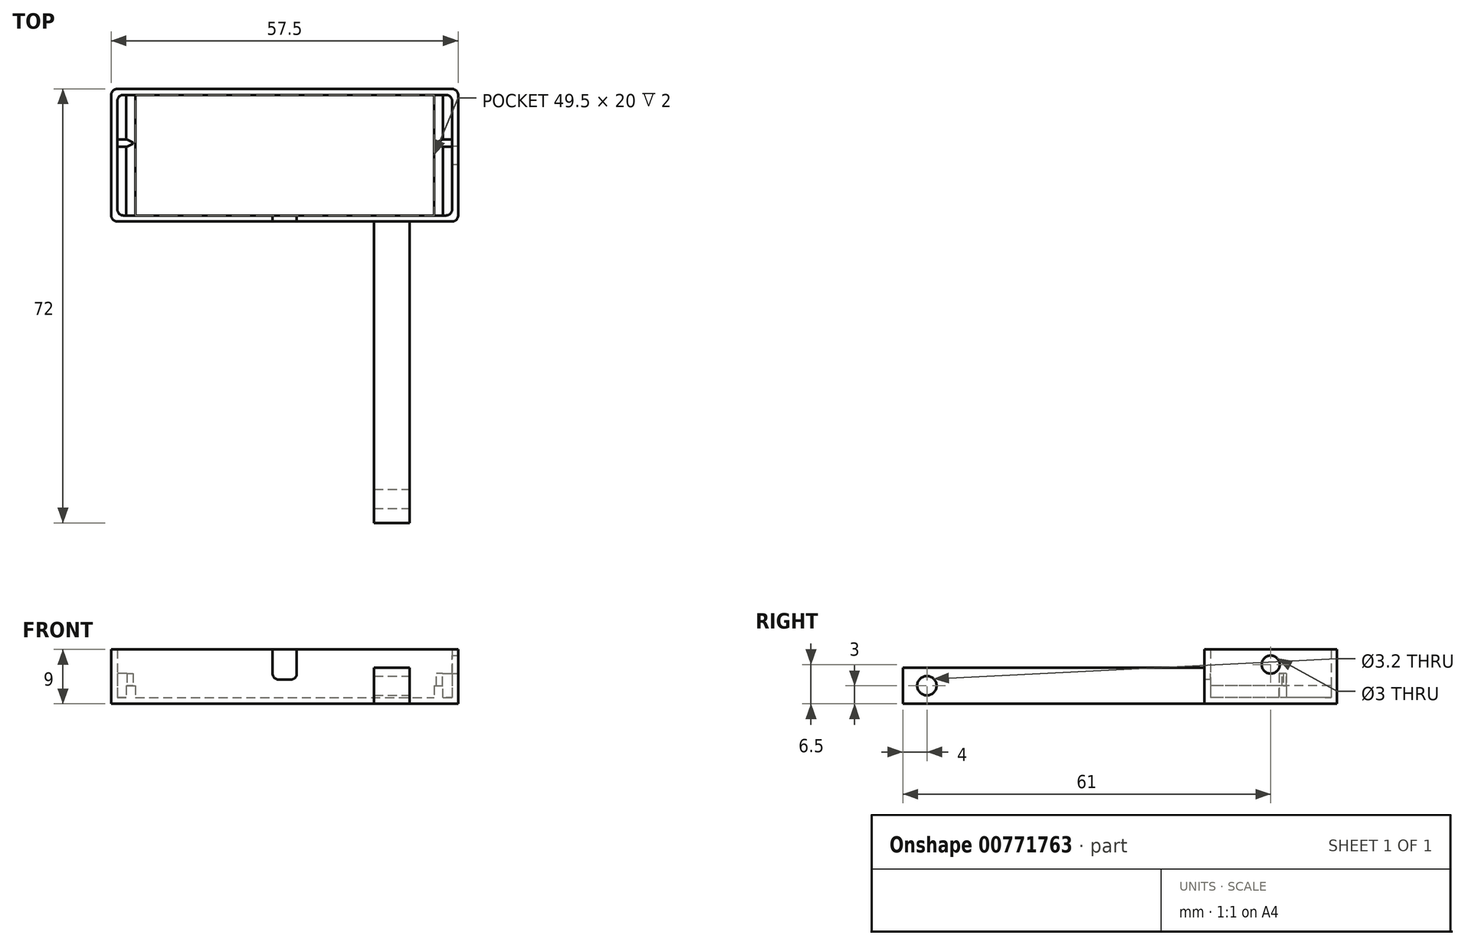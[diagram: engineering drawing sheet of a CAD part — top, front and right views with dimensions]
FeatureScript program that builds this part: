
annotation { "Feature Type Name" : "Feature", "Feature Type Description" : "" }
export const myFeature = defineFeature(function(context is Context, id is Id, definition is map)
    precondition{}
    {
        {
            var Q0;
            Q0=qCreatedBy(makeId("Top.planeOp"),FACE);
            var sketch = newSketch(context, id + "F0", { "sketchPlane" : qUnion([Q0])});
            skLineSegment(sketch, "E0.bottom", {"start": v(-27.75, 10) * mm, "end": v(27.75, 10) * mm});
            skLineSegment(sketch, "E0.top", {"start": v(-27.75, -10) * mm, "end": v(27.75, -10) * mm});
            skLineSegment(sketch, "E0.left", {"start": v(-27.75, 10) * mm, "end": v(-27.75, -10) * mm});
            skLineSegment(sketch, "E0.right", {"start": v(27.75, 10) * mm, "end": v(27.75, -10) * mm});
            skLineSegment(sketch, "E1", {"start": v(0, 10) * mm, "end": v(0, -10) * mm, "construction": true});
            skLineSegment(sketch, "E2", {"start": v(-27.75, 0) * mm, "end": v(27.75, 0) * mm, "construction": true});
            skLineSegment(sketch, "E3.0", {"start": v(-28.75, 11) * mm, "end": v(28.75, 11) * mm});
            skLineSegment(sketch, "E3.1", {"start": v(-28.75, 11) * mm, "end": v(-28.75, -11) * mm});
            skLineSegment(sketch, "E3.2", {"start": v(-28.75, -11) * mm, "end": v(28.75, -11) * mm});
            skLineSegment(sketch, "E3.3", {"start": v(28.75, 11) * mm, "end": v(28.75, -11) * mm});
            skSolve(sketch);
        }
        {
            var Q0;
            Q0 = qSketchRegion(id + "F0", true);
            extrude(context, id + "F1", {"entities" : qUnion([Q0]), "depth" : 9 * mm, "offsetDistance" : 25 * mm});
        }
        {
            var Q0;
            Q0=qCreatedBy(makeId("Top.planeOp"),FACE);
            var sketch = newSketch(context, id + "F2", { "sketchPlane" : qUnion([Q0])});
            skLineSegment(sketch, "E4.bottom", {"start": v(-28.75, 11) * mm, "end": v(28.75, 11) * mm});
            skLineSegment(sketch, "E4.top", {"start": v(-28.75, -11) * mm, "end": v(28.75, -11) * mm});
            skLineSegment(sketch, "E4.left", {"start": v(-28.75, 11) * mm, "end": v(-28.75, -11) * mm});
            skLineSegment(sketch, "E4.right", {"start": v(28.75, 11) * mm, "end": v(28.75, -11) * mm});
            skSolve(sketch);
        }
        {
            var Q0;
            Q0 = qSketchRegion(id + "F2", true);
            extrude(context, id + "F3", {"entities" : qUnion([Q0]), "operationType" : NewBodyOperationType.ADD, "depth" : 1 * mm, "offsetDistance" : 25 * mm});
        }
        {
            var Q0;
            Q0=makeQuery(id+"F1.opExtrude","SWEPT_FACE",FACE,{"disambiguationData":[OSD([sQuery(id+"F0.wireOp",EDGE,"E3.2")])]});
            var sketch = newSketch(context, id + "F4", { "sketchPlane" : qUnion([Q0])});
            skLineSegment(sketch, "E5", {"start": v(-2, 9) * mm, "end": v(-2, 5) * mm});
            skLineSegment(sketch, "E6.MirrorCS", {"start": v(2, 9) * mm, "end": v(2, 5) * mm});
            skLineSegment(sketch, "E7", {"start": v(-1, 4) * mm, "end": v(1, 4) * mm});
            skPoint(sketch, "E8.visualSharp", {"position": v(-2, 4) * mm});
            skArc(sketch, "E8.filletArc", {"start": v(-2, 5) * mm, "mid": v(-1.7, 4.3) * mm, "end": v(-1, 4) * mm});
            skPoint(sketch, "E9.visualSharp", {"position": v(2, 4) * mm});
            skArc(sketch, "E9.filletArc", {"start": v(1, 4) * mm, "mid": v(1.7, 4.3) * mm, "end": v(2, 5) * mm});
            skLineSegment(sketch, "E10", {"start": v(2, 9) * mm, "end": v(-2, 9) * mm});
            skSolve(sketch);
        }
        {
            var Q0;
            Q0 = qSketchRegion(id + "F4", true);
            var Q1;
            Q1=makeQuery(id+"F1.opExtrude","SWEPT_FACE",FACE,{"disambiguationData":[OSD([sQuery(id+"F0.wireOp",EDGE,"E0.top")])]});
            extrude(context, id + "F5", {"entities" : qUnion([Q0]), "operationType" : NewBodyOperationType.REMOVE, "endBound" : BoundingType.UP_TO_SURFACE, "oppositeDirection" : true, "depth" : 25 * mm, "endBoundEntityFace" : qUnion([Q1]), "offsetDistance" : 25 * mm});
        }
        {
            var Q0;
            Q0=makeQuery(id+"F1.opExtrude","SWEPT_FACE",FACE,{"disambiguationData":[OSD([sQuery(id+"F0.wireOp",EDGE,"E3.2")])]});
            var sketch = newSketch(context, id + "F6", { "sketchPlane" : qUnion([Q0])});
            skLineSegment(sketch, "E11", {"start": v(17.75, 9) * mm, "end": v(17.75, 0) * mm, "construction": true});
            skLineSegment(sketch, "E12", {"start": v(14.8, 6) * mm, "end": v(14.8, 0) * mm});
            skLineSegment(sketch, "E13.MirrorCS", {"start": v(20.7, 6) * mm, "end": v(20.7, 0) * mm});
            skLineSegment(sketch, "E14", {"start": v(14.8, 6) * mm, "end": v(20.7, 6) * mm});
            skLineSegment(sketch, "E15", {"start": v(20.7, 0) * mm, "end": v(14.8, 0) * mm});
            skSolve(sketch);
        }
        {
            var Q0;
            Q0 = qSketchRegion(id + "F6", true);
            extrude(context, id + "F7", {"entities" : qUnion([Q0]), "operationType" : NewBodyOperationType.ADD, "depth" : 50 * mm, "offsetDistance" : 25 * mm});
        }
        {
            var Q0;
            Q0=makeQuery(id+"F7.opExtrude","SWEPT_FACE",FACE,{"disambiguationData":[OSD([sQuery(id+"F6.wireOp",EDGE,"E13.MirrorCS")])]});
            var sketch = newSketch(context, id + "F8", { "sketchPlane" : qUnion([Q0])});
            skCircle(sketch, "E16", {"center": v(-57, 3) * mm, "radius": 1.6 * mm});
            skLineSegment(sketch, "E17", {"start": v(-61, 3) * mm, "end": v(-11, 3) * mm, "construction": true});
            skSolve(sketch);
        }
        {
            var Q0;
            Q0 = qSketchRegion(id + "F8", true);
            var Q1;
            Q1=makeQuery(id+"F7.opExtrude","SWEPT_FACE",FACE,{"disambiguationData":[OSD([sQuery(id+"F6.wireOp",EDGE,"E12")])]});
            extrude(context, id + "F9", {"entities" : qUnion([Q0]), "operationType" : NewBodyOperationType.REMOVE, "endBound" : BoundingType.UP_TO_SURFACE, "oppositeDirection" : true, "depth" : 25 * mm, "endBoundEntityFace" : qUnion([Q1]), "offsetDistance" : 25 * mm});
        }
        {
            var Q0;
            Q0=makeQuery(id+"F3.opExtrude","CAP_FACE",FACE,{"disambiguationData":[OSD([sQuery(id+"F2.wireOp",EDGE,"E4.bottom"),sQuery(id+"F2.wireOp",EDGE,"E4.top"),sQuery(id+"F2.wireOp",EDGE,"E4.left"),sQuery(id+"F2.wireOp",EDGE,"E4.right")])],"isStart":false});
            var sketch = newSketch(context, id + "F10", { "sketchPlane" : qUnion([Q0])});
            skLineSegment(sketch, "E18.bottom", {"start": v(-26.25, 10) * mm, "end": v(-24.75, 10) * mm});
            skLineSegment(sketch, "E18.top", {"start": v(-26.25, -10) * mm, "end": v(-24.75, -10) * mm});
            skLineSegment(sketch, "E18.left", {"start": v(-26.25, 10) * mm, "end": v(-26.25, -10) * mm});
            skLineSegment(sketch, "E18.right", {"start": v(-24.75, 10) * mm, "end": v(-24.75, -10) * mm});
            skLineSegment(sketch, "E19.MirrorCS", {"start": v(26.25, -10) * mm, "end": v(24.75, -10) * mm});
            skLineSegment(sketch, "E20.MirrorCS", {"start": v(24.75, 10) * mm, "end": v(24.75, -10) * mm});
            skLineSegment(sketch, "E21.MirrorCS", {"start": v(26.25, 10) * mm, "end": v(26.25, -10) * mm});
            skLineSegment(sketch, "E22.MirrorCS", {"start": v(26.25, 10) * mm, "end": v(24.75, 10) * mm});
            skSolve(sketch);
        }
        {
            var Q0;
            Q0 = qSketchRegion(id + "F10", true);
            extrude(context, id + "F11", {"entities" : qUnion([Q0]), "operationType" : NewBodyOperationType.ADD, "depth" : 2 * mm, "offsetDistance" : 25 * mm});
        }
        {
            var Q0;
            Q0=makeQuery(id+"F1.opExtrude","SWEPT_EDGE",EDGE,{"disambiguationData":[OSD([sQuery(id+"F0.wireOp",EDGE,"E3.1"),sQuery(id+"F0.wireOp",EDGE,"E3.2")])]});
            var Q1;
            Q1=makeQuery(id+"F1.opExtrude","SWEPT_EDGE",EDGE,{"disambiguationData":[OSD([sQuery(id+"F0.wireOp",EDGE,"E3.2"),sQuery(id+"F0.wireOp",EDGE,"E3.3")])]});
            var Q2;
            Q2=makeQuery(id+"F1.opExtrude","SWEPT_EDGE",EDGE,{"disambiguationData":[OSD([sQuery(id+"F0.wireOp",EDGE,"E3.0"),sQuery(id+"F0.wireOp",EDGE,"E3.3")])]});
            var Q3;
            Q3=makeQuery(id+"F1.opExtrude","SWEPT_EDGE",EDGE,{"disambiguationData":[OSD([sQuery(id+"F0.wireOp",EDGE,"E3.0"),sQuery(id+"F0.wireOp",EDGE,"E3.1")])]});
            fillet(context, id + "F12", {"entities" : qUnion([Q0, Q1, Q2, Q3]), "radius" : 1 * mm, "tangentPropagation" : true, "allowEdgeOverflow" : false});
        }
        {
            var Q0;
            Q0=makeQuery(id+"F1.opExtrude","SWEPT_EDGE",EDGE,{"disambiguationData":[OSD([sQuery(id+"F0.wireOp",EDGE,"E0.bottom"),sQuery(id+"F0.wireOp",EDGE,"E0.left")])]});
            var Q1;
            Q1=makeQuery(id+"F1.opExtrude","SWEPT_EDGE",EDGE,{"disambiguationData":[OSD([sQuery(id+"F0.wireOp",EDGE,"E0.bottom"),sQuery(id+"F0.wireOp",EDGE,"E0.right")])]});
            var Q2;
            Q2=makeQuery(id+"F1.opExtrude","SWEPT_EDGE",EDGE,{"disambiguationData":[OSD([sQuery(id+"F0.wireOp",EDGE,"E0.top"),sQuery(id+"F0.wireOp",EDGE,"E0.right")])]});
            var Q3;
            Q3=makeQuery(id+"F1.opExtrude","SWEPT_EDGE",EDGE,{"disambiguationData":[OSD([sQuery(id+"F0.wireOp",EDGE,"E0.top"),sQuery(id+"F0.wireOp",EDGE,"E0.left")])]});
            fillet(context, id + "F13", {"entities" : qUnion([Q0, Q1, Q2, Q3]), "radius" : 1 * mm, "tangentPropagation" : true, "allowEdgeOverflow" : false});
        }
        {
            var Q0;
            Q0=makeQuery(id+"F1.opExtrude","SWEPT_FACE",FACE,{"disambiguationData":[OSD([sQuery(id+"F0.wireOp",EDGE,"E3.3")])]});
            var sketch = newSketch(context, id + "F14", { "sketchPlane" : qUnion([Q0])});
            skCircle(sketch, "E23", {"center": v(0, 6.5) * mm, "radius": 1.5 * mm});
            skSolve(sketch);
        }
        {
            var Q0;
            Q0 = qSketchRegion(id + "F14", true);
            var Q1;
            Q1=makeQuery(id+"F1.opExtrude","SWEPT_FACE",FACE,{"disambiguationData":[OSD([sQuery(id+"F0.wireOp",EDGE,"E0.right")])]});
            extrude(context, id + "F15", {"entities" : qUnion([Q0]), "operationType" : NewBodyOperationType.REMOVE, "endBound" : BoundingType.UP_TO_SURFACE, "oppositeDirection" : true, "depth" : 25 * mm, "endBoundEntityFace" : qUnion([Q1]), "offsetDistance" : 25 * mm});
        }
        {
            var Q0;
            Q0=makeQuery(id+"F11.boolean.opBoolean","SPLIT",FACE,{"disambiguationData":[TD([makeQuery(id+"F11.opExtrude","SWEPT_FACE",FACE,{"disambiguationData":[OSD([sQuery(id+"F10.wireOp",EDGE,"E18.right")])]})])],"derivedFrom":makeQuery(id+"F3.opExtrude","CAP_FACE",FACE,{"disambiguationData":[OSD([sQuery(id+"F2.wireOp",EDGE,"E4.bottom"),sQuery(id+"F2.wireOp",EDGE,"E4.top"),sQuery(id+"F2.wireOp",EDGE,"E4.left"),sQuery(id+"F2.wireOp",EDGE,"E4.right")])],"isStart":false})});
            var sketch = newSketch(context, id + "F16", { "sketchPlane" : qUnion([Q0])});
            skLineSegment(sketch, "E24", {"start": v(24.9, 2) * mm, "end": v(29.4, 2) * mm, "construction": true});
            skLineSegment(sketch, "E25", {"start": v(25.15, 2.6) * mm, "end": v(27.75, 2.6) * mm});
            skLineSegment(sketch, "E26.MirrorCS", {"start": v(25.15, 1.4) * mm, "end": v(27.75, 1.4) * mm});
            skLineSegment(sketch, "E27", {"start": v(27.75, 2.6) * mm, "end": v(27.75, 1.4) * mm});
            skPoint(sketch, "E28.visualSharp", {"position": v(25.15, 2.6) * mm});
            skPoint(sketch, "E29.visualSharp", {"position": v(25.15, 1.4) * mm});
            skLineSegment(sketch, "E30.MirrorCS", {"start": v(27.75, 1.4) * mm, "end": v(27.75, 2.6) * mm});
            skLineSegment(sketch, "E31", {"start": v(25.15, 2.6) * mm, "end": v(25.15, 1.4) * mm});
            skLineSegment(sketch, "E32.MirrorCS", {"start": v(25.15, 1.4) * mm, "end": v(25.15, 2.6) * mm});
            skLineSegment(sketch, "E33.MirrorCS", {"start": v(-27.75, 2.6) * mm, "end": v(-27.75, 1.4) * mm});
            skPoint(sketch, "E34.MirrorP", {"position": v(-25.15, 1.4) * mm});
            skPoint(sketch, "E35.MirrorP", {"position": v(-25.15, 2.6) * mm});
            skLineSegment(sketch, "E36.MirrorCS", {"start": v(-25.15, 1.4) * mm, "end": v(-25.15, 2.6) * mm});
            skLineSegment(sketch, "E37.MirrorCS", {"start": v(-25.15, 2.6) * mm, "end": v(-27.75, 2.6) * mm});
            skLineSegment(sketch, "E38.MirrorCS", {"start": v(-27.75, 1.4) * mm, "end": v(-27.75, 2.6) * mm});
            skLineSegment(sketch, "E39.MirrorCS", {"start": v(-25.15, 2.6) * mm, "end": v(-25.15, 1.4) * mm});
            skLineSegment(sketch, "E40.MirrorCS", {"start": v(-25.15, 1.4) * mm, "end": v(-27.75, 1.4) * mm});
            skLineSegment(sketch, "E41.MirrorCS", {"start": v(-24.9, 2) * mm, "end": v(-29.4, 2) * mm, "construction": true});
            skSolve(sketch);
        }
        {
            var Q0;
            Q0 = qSketchRegion(id + "F16", true);
            extrude(context, id + "F17", {"entities" : qUnion([Q0]), "operationType" : NewBodyOperationType.ADD, "depth" : 4 * mm, "offsetDistance" : 25 * mm});
        }
        {
            var Q0;
            Q0=makeQuery(id+"F17.opExtrude","SWEPT_EDGE",EDGE,{"disambiguationData":[OSD([sQuery(id+"F16.wireOp",EDGE,"E39.MirrorCS"),sQuery(id+"F16.wireOp",EDGE,"E37.MirrorCS")])]});
            var Q1;
            Q1=makeQuery(id+"F17.opExtrude","SWEPT_EDGE",EDGE,{"disambiguationData":[OSD([sQuery(id+"F16.wireOp",EDGE,"E39.MirrorCS"),sQuery(id+"F16.wireOp",EDGE,"E40.MirrorCS")])]});
            chamfer(context, id + "F18", {"entities" : qUnion([Q0, Q1]), "chamferType" : ChamferType.TWO_OFFSETS, "width1" : 1 * mm, "oppositeDirection" : false, "width2" : .5 * mm, "tangentPropagation" : true});
        }
        {
            var Q0;
            Q0=makeQuery(id+"F17.opExtrude","SWEPT_EDGE",EDGE,{"disambiguationData":[OSD([sQuery(id+"F16.wireOp",EDGE,"E32.MirrorCS"),sQuery(id+"F16.wireOp",EDGE,"E25")])]});
            var Q1;
            Q1=makeQuery(id+"F17.opExtrude","SWEPT_EDGE",EDGE,{"disambiguationData":[OSD([sQuery(id+"F16.wireOp",EDGE,"E32.MirrorCS"),sQuery(id+"F16.wireOp",EDGE,"E26.MirrorCS")])]});
            chamfer(context, id + "F19", {"entities" : qUnion([Q0, Q1]), "chamferType" : ChamferType.TWO_OFFSETS, "width1" : .5 * mm, "oppositeDirection" : false, "width2" : 1 * mm, "tangentPropagation" : true});
        }
    });
